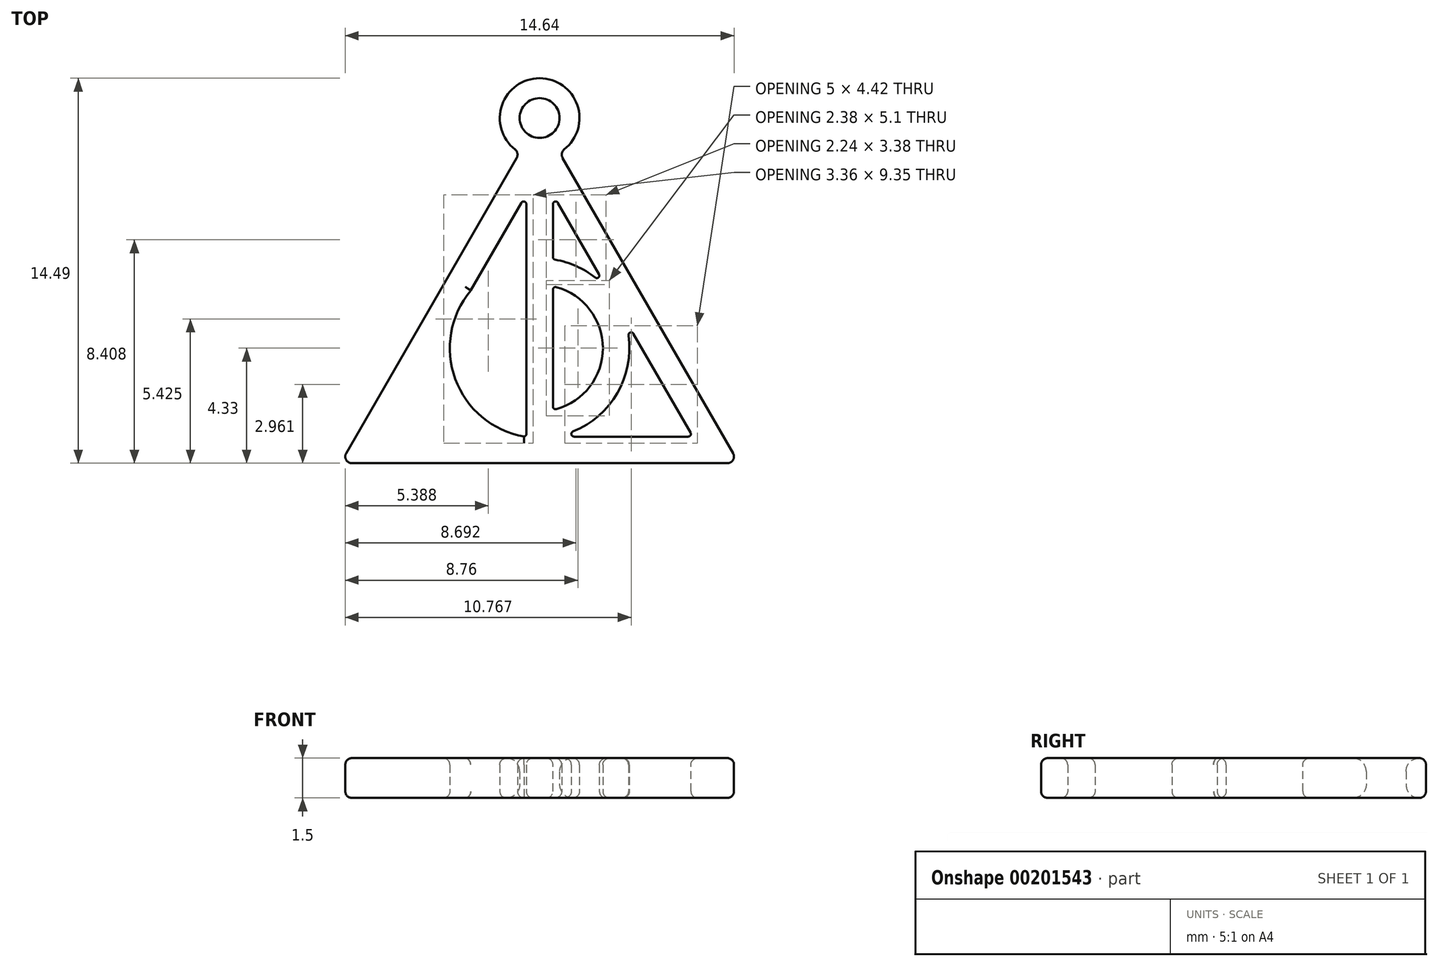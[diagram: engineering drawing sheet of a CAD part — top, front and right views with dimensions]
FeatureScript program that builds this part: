
annotation { "Feature Type Name" : "Feature", "Feature Type Description" : "" }
export const myFeature = defineFeature(function(context is Context, id is Id, definition is map)
    precondition{}
    {
        {
            var Q0;
            Q0=qCreatedBy(makeId("Top.planeOp"),FACE);
            var sketch = newSketch(context, id + "F0", { "sketchPlane" : qUnion([Q0])});
            skLineSegment(sketch, "E0", {"start": v(0, 0) * mm, "end": v(-7.5, -13) * mm});
            skLineSegment(sketch, "E1", {"start": v(-7.5, -13) * mm, "end": v(7.5, -13) * mm});
            skLineSegment(sketch, "E2", {"start": v(7.5, -13) * mm, "end": v(0, 0) * mm});
            skCircle(sketch, "E3", {"center": v(0, 0) * mm, "radius": 1.5 * mm});
            skCircle(sketch, "E4", {"center": v(0, 0) * mm, "radius": 0.75 * mm});
            skLineSegment(sketch, "E5.0", {"start": v(0, -2) * mm, "end": v(-5.77, -12) * mm});
            skLineSegment(sketch, "E5.1", {"start": v(5.77, -12) * mm, "end": v(0, -2) * mm});
            skLineSegment(sketch, "E5.2", {"start": v(-5.77, -12) * mm, "end": v(5.77, -12) * mm});
            skLineSegment(sketch, "E6", {"start": v(0, 0) * mm, "end": v(0, -13) * mm, "construction": true});
            skLineSegment(sketch, "E7", {"start": v(-0.5, -2.87) * mm, "end": v(-0.5, -12) * mm});
            skLineSegment(sketch, "E8.MirrorCS", {"start": v(0.5, -2.87) * mm, "end": v(0.5, -12) * mm});
            skCircle(sketch, "E9", {"center": v(0, -8.66) * mm, "radius": 3.38 * mm});
            skLineSegment(sketch, "E10", {"start": v(0, -8.66) * mm, "end": v(-2.93, -6.97) * mm, "construction": true});
            skPoint(sketch, "E11", {"position": v(0, -12.04) * mm});
            skCircle(sketch, "E12.0", {"center": v(0, -8.66) * mm, "radius": 2.38 * mm});
            skSolve(sketch);
        }
        {
            var Q0;
            {var subQ0=sQuery(id+"F0.wireOp",EDGE,"E3");var subQ1=sQuery(id+"F0.wireOp",EDGE,"E0");var subQ2=makeQuery(id+"F0.imprint","INTERSECT",VERTEX,{"derivedFrom":[subQ1,subQ0]});Q0=makeQuery(id+"F0.imprint","IMPRINT",FACE,{"disambiguationData":[TD([[makeQuery(id+"F0.imprint","IMPRINT",EDGE,{"disambiguationData":[TD([[subQ2,1.0]])],"derivedFrom":subQ1}),-1.0]])]});}
            var Q1;
            {var subQ0=sQuery(id+"F0.wireOp",EDGE,"E3");var subQ1=sQuery(id+"F0.wireOp",EDGE,"E0");var subQ2=makeQuery(id+"F0.imprint","INTERSECT",VERTEX,{"derivedFrom":[subQ1,subQ0]});Q1=makeQuery(id+"F0.imprint","IMPRINT",FACE,{"disambiguationData":[TD([[makeQuery(id+"F0.imprint","IMPRINT",EDGE,{"disambiguationData":[TD([[subQ2,1.0]])],"derivedFrom":subQ1}),1.0]])]});}
            var Q2;
            {var subQ1=sQuery(id+"F0.wireOp",EDGE,"E5.1");var subQ5=sQuery(id+"F0.wireOp",EDGE,"E5.0");var subQ6=makeQuery(id+"F0.imprint","INTERSECT",VERTEX,{"derivedFrom":[subQ5,subQ1]});Q2=makeQuery(id+"F0.imprint","IMPRINT",FACE,{"disambiguationData":[TD([[makeQuery(id+"F0.imprint","IMPRINT",EDGE,{"disambiguationData":[TD([[subQ6,-1.0]])],"derivedFrom":subQ5}),1.0]])]});}
            var Q3;
            {var subQ0=sQuery(id+"F0.wireOp",EDGE,"E12.0");var subQ1=sQuery(id+"F0.wireOp",EDGE,"E7");var subQ2=makeQuery(id+"F0.imprint","INTERSECT",VERTEX,{"disambiguationData":[OD(0.0)],"derivedFrom":[subQ1,subQ0]});Q3=makeQuery(id+"F0.imprint","IMPRINT",FACE,{"disambiguationData":[TD([[makeQuery(id+"F0.imprint","IMPRINT",EDGE,{"disambiguationData":[TD([[subQ2,-1.0]])],"derivedFrom":subQ1}),1.0]])]});}
            var Q4;
            {var subQ10=sQuery(id+"F0.wireOp",EDGE,"E1");Q4=makeQuery(id+"F0.imprint","IMPRINT",FACE,{"disambiguationData":[TD([[makeQuery(id+"F0.imprint","IMPRINT",EDGE,{"derivedFrom":subQ10}),1.0]])]});}
            var Q5;
            {var subQ0=sQuery(id+"F0.wireOp",EDGE,"E9");var subQ9=sQuery(id+"F0.wireOp",EDGE,"E5.0");var subQ10=makeQuery(id+"F0.imprint","INTERSECT",VERTEX,{"disambiguationData":[OD(0.0)],"derivedFrom":[subQ9,subQ0]});Q5=makeQuery(id+"F0.imprint","IMPRINT",FACE,{"disambiguationData":[TD([[makeQuery(id+"F0.imprint","IMPRINT",EDGE,{"disambiguationData":[TD([[subQ10,-1.0]])],"derivedFrom":subQ9}),1.0]])]});}
            var Q6;
            {var subQ5=sQuery(id+"F0.wireOp",EDGE,"E9");var subQ9=sQuery(id+"F0.wireOp",EDGE,"E5.1");var subQ11=makeQuery(id+"F0.imprint","INTERSECT",VERTEX,{"disambiguationData":[OD(0.0)],"derivedFrom":[subQ9,subQ5]});Q6=makeQuery(id+"F0.imprint","IMPRINT",FACE,{"disambiguationData":[TD([[makeQuery(id+"F0.imprint","IMPRINT",EDGE,{"disambiguationData":[TD([[subQ11,-1.0]])],"derivedFrom":subQ9}),1.0]])]});}
            var Q7;
            {var subQ0=sQuery(id+"F0.wireOp",EDGE,"E9");var subQ1=sQuery(id+"F0.wireOp",EDGE,"E7");var subQ2=makeQuery(id+"F0.imprint","INTERSECT",VERTEX,{"derivedFrom":[subQ1,subQ0]});Q7=makeQuery(id+"F0.imprint","IMPRINT",FACE,{"disambiguationData":[TD([[makeQuery(id+"F0.imprint","IMPRINT",EDGE,{"disambiguationData":[TD([[subQ2,-1.0]])],"derivedFrom":subQ1}),1.0]])]});}
            var Q8;
            {var subQ0=sQuery(id+"F0.wireOp",EDGE,"E7");var subQ1=sQuery(id+"F0.wireOp",EDGE,"E5.2");var subQ2=makeQuery(id+"F0.imprint","INTERSECT",VERTEX,{"derivedFrom":[subQ1,subQ0]});Q8=makeQuery(id+"F0.imprint","IMPRINT",FACE,{"disambiguationData":[TD([[makeQuery(id+"F0.imprint","IMPRINT",EDGE,{"disambiguationData":[TD([[subQ2,-1.0]])],"derivedFrom":subQ1}),1.0]])]});}
            var Q9;
            {var subQ0=sQuery(id+"F0.wireOp",EDGE,"E5.2");var subQ1=makeQuery(id+"F0.imprint","INTERSECT",VERTEX,{"derivedFrom":[subQ0,sQuery(id+"F0.wireOp",EDGE,"E7")]});Q9=makeQuery(id+"F0.imprint","IMPRINT",FACE,{"disambiguationData":[TD([[makeQuery(id+"F0.imprint","IMPRINT",EDGE,{"disambiguationData":[TD([[subQ1,1.0]])],"derivedFrom":subQ0}),-1.0]])]});}
            var Q10;
            {var subQ0=sQuery(id+"F0.wireOp",EDGE,"E9");var subQ1=sQuery(id+"F0.wireOp",EDGE,"E5.0");var subQ2=makeQuery(id+"F0.imprint","INTERSECT",VERTEX,{"disambiguationData":[OD(0.0)],"derivedFrom":[subQ1,subQ0]});Q10=makeQuery(id+"F0.imprint","IMPRINT",FACE,{"disambiguationData":[TD([[makeQuery(id+"F0.imprint","IMPRINT",EDGE,{"disambiguationData":[TD([[subQ2,-1.0]])],"derivedFrom":subQ1}),-1.0]])]});}
            var Q11;
            {var subQ0=sQuery(id+"F0.wireOp",EDGE,"E9");var subQ1=sQuery(id+"F0.wireOp",EDGE,"E5.1");var subQ2=makeQuery(id+"F0.imprint","INTERSECT",VERTEX,{"disambiguationData":[OD(0.0)],"derivedFrom":[subQ1,subQ0]});Q11=makeQuery(id+"F0.imprint","IMPRINT",FACE,{"disambiguationData":[TD([[makeQuery(id+"F0.imprint","IMPRINT",EDGE,{"disambiguationData":[TD([[subQ2,-1.0]])],"derivedFrom":subQ1}),-1.0]])]});}
            extrude(context, id + "F1", {"entities" : qUnion([Q0, Q1, Q2, Q3, Q4, Q5, Q6, Q7, Q8, Q9, Q10, Q11]), "depth" : 1.5 * mm});
        }
        {
            var Q0;
            Q0=makeQuery(id+"F1.opExtrude","SWEPT_EDGE",EDGE,{"disambiguationData":[OSD([sQuery(id+"F0.wireOp",EDGE,"E2"),sQuery(id+"F0.wireOp",EDGE,"E3")])]});
            var Q1;
            Q1=makeQuery(id+"F1.opExtrude","SWEPT_EDGE",EDGE,{"disambiguationData":[OSD([sQuery(id+"F0.wireOp",EDGE,"E0"),sQuery(id+"F0.wireOp",EDGE,"E3")])]});
            var Q2;
            Q2=makeQuery(id+"F1.opExtrude","SWEPT_EDGE",EDGE,{"disambiguationData":[OSD([sQuery(id+"F0.wireOp",EDGE,"E0"),sQuery(id+"F0.wireOp",EDGE,"E1")])]});
            var Q3;
            Q3=makeQuery(id+"F1.opExtrude","SWEPT_EDGE",EDGE,{"disambiguationData":[OSD([sQuery(id+"F0.wireOp",EDGE,"E1"),sQuery(id+"F0.wireOp",EDGE,"E2")])]});
            fillet(context, id + "F2", {"entities" : qUnion([Q0, Q1, Q2, Q3]), "radius" : .25 * mm, "tangentPropagation" : true, "allowEdgeOverflow" : false});
        }
        {
            var Q0;
            Q0=makeQuery(id+"F1.opExtrude","CAP_EDGE",EDGE,{"disambiguationData":[OSD([sQuery(id+"F0.wireOp",EDGE,"E3")])],"isStart":false});
            var Q1;
            Q1=makeQuery(id+"F1.opExtrude","CAP_EDGE",EDGE,{"disambiguationData":[OSD([sQuery(id+"F0.wireOp",EDGE,"E3")])],"isStart":true});
            fillet(context, id + "F3", {"entities" : qUnion([Q0, Q1]), "radius" : .25 * mm, "tangentPropagation" : true, "allowEdgeOverflow" : false});
        }
        {
            var Q0;
            Q0=makeQuery(id+"F1.opExtrude","CAP_EDGE",EDGE,{"disambiguationData":[OSD([sQuery(id+"F0.wireOp",EDGE,"E4")])],"isStart":false});
            var Q1;
            Q1=makeQuery(id+"F1.opExtrude","CAP_EDGE",EDGE,{"disambiguationData":[OSD([sQuery(id+"F0.wireOp",EDGE,"E4")])],"isStart":true});
            fillet(context, id + "F4", {"entities" : qUnion([Q0, Q1]), "radius" : .5 * mm, "tangentPropagation" : true, "allowEdgeOverflow" : false});
        }
        {
            var Q0;
            Q0=makeQuery(id+"F1.opExtrude","SWEPT_EDGE",EDGE,{"disambiguationData":[OSD([sQuery(id+"F0.wireOp",EDGE,"E5.0"),sQuery(id+"F0.wireOp",EDGE,"E7")])]});
            var Q1;
            {var subQ0=sQuery(id+"F0.wireOp",EDGE,"E9");var subQ1=sQuery(id+"F0.wireOp",EDGE,"E5.0");Q1=makeQuery(id+"F1.opExtrude","SWEPT_EDGE",EDGE,{"disambiguationData":[OSD([subQ1,subQ0]),TDD([makeQuery(id+"F0.imprint","INTERSECT",VERTEX,{"disambiguationData":[OD(0.0)],"derivedFrom":[subQ1,subQ0]})])]});}
            var Q2;
            Q2=makeQuery(id+"F1.opExtrude","SWEPT_EDGE",EDGE,{"disambiguationData":[OSD([sQuery(id+"F0.wireOp",EDGE,"E7"),sQuery(id+"F0.wireOp",EDGE,"E9")])]});
            var Q3;
            Q3=makeQuery(id+"F1.opExtrude","SWEPT_EDGE",EDGE,{"disambiguationData":[OSD([sQuery(id+"F0.wireOp",EDGE,"E5.1"),sQuery(id+"F0.wireOp",EDGE,"E8.MirrorCS")])]});
            var Q4;
            Q4=makeQuery(id+"F1.opExtrude","SWEPT_EDGE",EDGE,{"disambiguationData":[OSD([sQuery(id+"F0.wireOp",EDGE,"E8.MirrorCS"),sQuery(id+"F0.wireOp",EDGE,"E9")])]});
            var Q5;
            {var subQ0=sQuery(id+"F0.wireOp",EDGE,"E9");var subQ1=sQuery(id+"F0.wireOp",EDGE,"E5.1");Q5=makeQuery(id+"F1.opExtrude","SWEPT_EDGE",EDGE,{"disambiguationData":[OSD([subQ1,subQ0]),TDD([makeQuery(id+"F0.imprint","INTERSECT",VERTEX,{"disambiguationData":[OD(1.0)],"derivedFrom":[subQ1,subQ0]})])]});}
            var Q6;
            Q6=makeQuery(id+"F1.opExtrude","SWEPT_EDGE",EDGE,{"disambiguationData":[OSD([sQuery(id+"F0.wireOp",EDGE,"E5.1"),sQuery(id+"F0.wireOp",EDGE,"E5.2")])]});
            var Q7;
            {var subQ0=sQuery(id+"F0.wireOp",EDGE,"E9");var subQ1=sQuery(id+"F0.wireOp",EDGE,"E5.1");Q7=makeQuery(id+"F1.opExtrude","SWEPT_EDGE",EDGE,{"disambiguationData":[OSD([subQ1,subQ0]),TDD([makeQuery(id+"F0.imprint","INTERSECT",VERTEX,{"disambiguationData":[OD(0.0)],"derivedFrom":[subQ1,subQ0]})])]});}
            var Q8;
            {var subQ0=sQuery(id+"F0.wireOp",EDGE,"E9");var subQ1=sQuery(id+"F0.wireOp",EDGE,"E5.0");Q8=makeQuery(id+"F1.opExtrude","SWEPT_EDGE",EDGE,{"disambiguationData":[OSD([subQ1,subQ0]),TDD([makeQuery(id+"F0.imprint","INTERSECT",VERTEX,{"disambiguationData":[OD(1.0)],"derivedFrom":[subQ1,subQ0]})])]});}
            var Q9;
            {var subQ0=sQuery(id+"F0.wireOp",EDGE,"E12.0");var subQ1=sQuery(id+"F0.wireOp",EDGE,"E7");Q9=makeQuery(id+"F1.opExtrude","SWEPT_EDGE",EDGE,{"disambiguationData":[OSD([subQ1,subQ0]),TDD([makeQuery(id+"F0.imprint","INTERSECT",VERTEX,{"disambiguationData":[OD(0.0)],"derivedFrom":[subQ1,subQ0]})])]});}
            var Q10;
            {var subQ0=sQuery(id+"F0.wireOp",EDGE,"E12.0");var subQ1=sQuery(id+"F0.wireOp",EDGE,"E8.MirrorCS");Q10=makeQuery(id+"F1.opExtrude","SWEPT_EDGE",EDGE,{"disambiguationData":[OSD([subQ1,subQ0]),TDD([makeQuery(id+"F0.imprint","INTERSECT",VERTEX,{"disambiguationData":[OD(0.0)],"derivedFrom":[subQ1,subQ0]})])]});}
            var Q11;
            {var subQ0=sQuery(id+"F0.wireOp",EDGE,"E12.0");var subQ1=sQuery(id+"F0.wireOp",EDGE,"E7");Q11=makeQuery(id+"F1.opExtrude","SWEPT_EDGE",EDGE,{"disambiguationData":[OSD([subQ1,subQ0]),TDD([makeQuery(id+"F0.imprint","INTERSECT",VERTEX,{"disambiguationData":[OD(1.0)],"derivedFrom":[subQ1,subQ0]})])]});}
            var Q12;
            Q12=makeQuery(id+"F1.opExtrude","SWEPT_EDGE",EDGE,{"disambiguationData":[OSD([sQuery(id+"F0.wireOp",EDGE,"E5.0"),sQuery(id+"F0.wireOp",EDGE,"E5.2")])]});
            var Q13;
            {var subQ0=sQuery(id+"F0.wireOp",EDGE,"E12.0");var subQ1=sQuery(id+"F0.wireOp",EDGE,"E8.MirrorCS");Q13=makeQuery(id+"F1.opExtrude","SWEPT_EDGE",EDGE,{"disambiguationData":[OSD([subQ1,subQ0]),TDD([makeQuery(id+"F0.imprint","INTERSECT",VERTEX,{"disambiguationData":[OD(1.0)],"derivedFrom":[subQ1,subQ0]})])]});}
            var Q14;
            {var subQ0=sQuery(id+"F0.wireOp",EDGE,"E9");var subQ1=sQuery(id+"F0.wireOp",EDGE,"E5.2");Q14=makeQuery(id+"F1.opExtrude","SWEPT_EDGE",EDGE,{"disambiguationData":[OSD([subQ1,subQ0]),TDD([makeQuery(id+"F0.imprint","INTERSECT",VERTEX,{"disambiguationData":[OD(1.0)],"derivedFrom":[subQ1,subQ0]})])]});}
            var Q15;
            {var subQ0=sQuery(id+"F0.wireOp",EDGE,"E9");var subQ1=sQuery(id+"F0.wireOp",EDGE,"E5.2");Q15=makeQuery(id+"F1.opExtrude","SWEPT_EDGE",EDGE,{"disambiguationData":[OSD([subQ1,subQ0]),TDD([makeQuery(id+"F0.imprint","INTERSECT",VERTEX,{"disambiguationData":[OD(0.0)],"derivedFrom":[subQ1,subQ0]})])]});}
            fillet(context, id + "F5", {"entities" : qUnion([Q0, Q1, Q2, Q3, Q4, Q5, Q6, Q7, Q8, Q9, Q10, Q11, Q12, Q13, Q14, Q15]), "radius" : .1 * mm, "tangentPropagation" : true, "allowEdgeOverflow" : false});
        }
        {
            var Q0;
            {var subQ0=sQuery(id+"F0.wireOp",EDGE,"E5.0");Q0=makeQuery(id+"F1.opExtrude","CAP_EDGE",EDGE,{"disambiguationData":[OSD([subQ0]),TDD([makeQuery(id+"F0.imprint","IMPRINT",EDGE,{"disambiguationData":[TD([[makeQuery(id+"F0.imprint","INTERSECT",VERTEX,{"derivedFrom":[subQ0,sQuery(id+"F0.wireOp",EDGE,"E7")]}),-1.0]])],"derivedFrom":subQ0})])],"isStart":false});}
            var Q1;
            {var subQ0=sQuery(id+"F0.wireOp",EDGE,"E5.0");Q1=makeQuery(id+"F1.opExtrude","CAP_EDGE",EDGE,{"disambiguationData":[OSD([subQ0]),TDD([makeQuery(id+"F0.imprint","IMPRINT",EDGE,{"disambiguationData":[TD([[makeQuery(id+"F0.imprint","INTERSECT",VERTEX,{"derivedFrom":[subQ0,sQuery(id+"F0.wireOp",EDGE,"E7")]}),-1.0]])],"derivedFrom":subQ0})])],"isStart":true});}
            var Q2;
            {var subQ0=sQuery(id+"F0.wireOp",EDGE,"E8.MirrorCS");Q2=makeQuery(id+"F1.opExtrude","CAP_EDGE",EDGE,{"disambiguationData":[OSD([subQ0]),TDD([makeQuery(id+"F0.imprint","IMPRINT",EDGE,{"disambiguationData":[TD([[makeQuery(id+"F0.imprint","INTERSECT",VERTEX,{"derivedFrom":[sQuery(id+"F0.wireOp",EDGE,"E5.1"),subQ0]}),-1.0]])],"derivedFrom":subQ0})])],"isStart":false});}
            var Q3;
            {var subQ0=sQuery(id+"F0.wireOp",EDGE,"E8.MirrorCS");Q3=makeQuery(id+"F1.opExtrude","CAP_EDGE",EDGE,{"disambiguationData":[OSD([subQ0]),TDD([makeQuery(id+"F0.imprint","IMPRINT",EDGE,{"disambiguationData":[TD([[makeQuery(id+"F0.imprint","INTERSECT",VERTEX,{"derivedFrom":[sQuery(id+"F0.wireOp",EDGE,"E5.1"),subQ0]}),-1.0]])],"derivedFrom":subQ0})])],"isStart":true});}
            var Q4;
            {var subQ0=sQuery(id+"F0.wireOp",EDGE,"E9");Q4=makeQuery(id+"F1.opExtrude","CAP_EDGE",EDGE,{"disambiguationData":[OSD([subQ0]),TDD([makeQuery(id+"F0.imprint","IMPRINT",EDGE,{"disambiguationData":[TD([[makeQuery(id+"F0.imprint","INTERSECT",VERTEX,{"disambiguationData":[OD(0.0)],"derivedFrom":[sQuery(id+"F0.wireOp",EDGE,"E5.1"),subQ0]}),1.0]])],"derivedFrom":subQ0})])],"isStart":true});}
            var Q5;
            {var subQ0=sQuery(id+"F0.wireOp",EDGE,"E12.0");var subQ1=sQuery(id+"F0.wireOp",EDGE,"E8.MirrorCS");Q5=makeQuery(id+"F1.opExtrude","CAP_EDGE",EDGE,{"disambiguationData":[OSD([subQ1]),TDD([makeQuery(id+"F0.imprint","IMPRINT",EDGE,{"disambiguationData":[TD([[makeQuery(id+"F0.imprint","INTERSECT",VERTEX,{"disambiguationData":[OD(0.0)],"derivedFrom":[subQ1,subQ0]}),-1.0]])],"derivedFrom":subQ1})])],"isStart":true});}
            var Q6;
            {var subQ0=sQuery(id+"F0.wireOp",EDGE,"E12.0");var subQ1=sQuery(id+"F0.wireOp",EDGE,"E7");Q6=makeQuery(id+"F1.opExtrude","CAP_EDGE",EDGE,{"disambiguationData":[OSD([subQ1]),TDD([makeQuery(id+"F0.imprint","IMPRINT",EDGE,{"disambiguationData":[TD([[makeQuery(id+"F0.imprint","INTERSECT",VERTEX,{"disambiguationData":[OD(0.0)],"derivedFrom":[subQ1,subQ0]}),-1.0]])],"derivedFrom":subQ1})])],"isStart":true});}
            var Q7;
            {var subQ0=sQuery(id+"F0.wireOp",EDGE,"E9");Q7=makeQuery(id+"F1.opExtrude","CAP_EDGE",EDGE,{"disambiguationData":[OSD([subQ0]),TDD([makeQuery(id+"F0.imprint","IMPRINT",EDGE,{"disambiguationData":[TD([[makeQuery(id+"F0.imprint","INTERSECT",VERTEX,{"disambiguationData":[OD(1.0)],"derivedFrom":[sQuery(id+"F0.wireOp",EDGE,"E5.0"),subQ0]}),-1.0]])],"derivedFrom":subQ0})])],"isStart":true});}
            var Q8;
            {var subQ0=sQuery(id+"F0.wireOp",EDGE,"E9");Q8=makeQuery(id+"F1.opExtrude","CAP_EDGE",EDGE,{"disambiguationData":[OSD([subQ0]),TDD([makeQuery(id+"F0.imprint","IMPRINT",EDGE,{"disambiguationData":[TD([[makeQuery(id+"F0.imprint","INTERSECT",VERTEX,{"disambiguationData":[OD(1.0)],"derivedFrom":[sQuery(id+"F0.wireOp",EDGE,"E5.0"),subQ0]}),-1.0]])],"derivedFrom":subQ0})])],"isStart":false});}
            var Q9;
            {var subQ0=sQuery(id+"F0.wireOp",EDGE,"E12.0");var subQ1=sQuery(id+"F0.wireOp",EDGE,"E7");Q9=makeQuery(id+"F1.opExtrude","CAP_EDGE",EDGE,{"disambiguationData":[OSD([subQ1]),TDD([makeQuery(id+"F0.imprint","IMPRINT",EDGE,{"disambiguationData":[TD([[makeQuery(id+"F0.imprint","INTERSECT",VERTEX,{"disambiguationData":[OD(0.0)],"derivedFrom":[subQ1,subQ0]}),-1.0]])],"derivedFrom":subQ1})])],"isStart":false});}
            var Q10;
            {var subQ0=sQuery(id+"F0.wireOp",EDGE,"E12.0");var subQ1=sQuery(id+"F0.wireOp",EDGE,"E8.MirrorCS");Q10=makeQuery(id+"F1.opExtrude","CAP_EDGE",EDGE,{"disambiguationData":[OSD([subQ1]),TDD([makeQuery(id+"F0.imprint","IMPRINT",EDGE,{"disambiguationData":[TD([[makeQuery(id+"F0.imprint","INTERSECT",VERTEX,{"disambiguationData":[OD(0.0)],"derivedFrom":[subQ1,subQ0]}),-1.0]])],"derivedFrom":subQ1})])],"isStart":false});}
            var Q11;
            {var subQ0=sQuery(id+"F0.wireOp",EDGE,"E9");Q11=makeQuery(id+"F1.opExtrude","CAP_EDGE",EDGE,{"disambiguationData":[OSD([subQ0]),TDD([makeQuery(id+"F0.imprint","IMPRINT",EDGE,{"disambiguationData":[TD([[makeQuery(id+"F0.imprint","INTERSECT",VERTEX,{"disambiguationData":[OD(0.0)],"derivedFrom":[sQuery(id+"F0.wireOp",EDGE,"E5.1"),subQ0]}),1.0]])],"derivedFrom":subQ0})])],"isStart":false});}
            fillet(context, id + "F6", {"entities" : qUnion([Q0, Q1, Q2, Q3, Q4, Q5, Q6, Q7, Q8, Q9, Q10, Q11]), "radius" : .25 * mm, "tangentPropagation" : true, "allowEdgeOverflow" : false});
        }
    });
